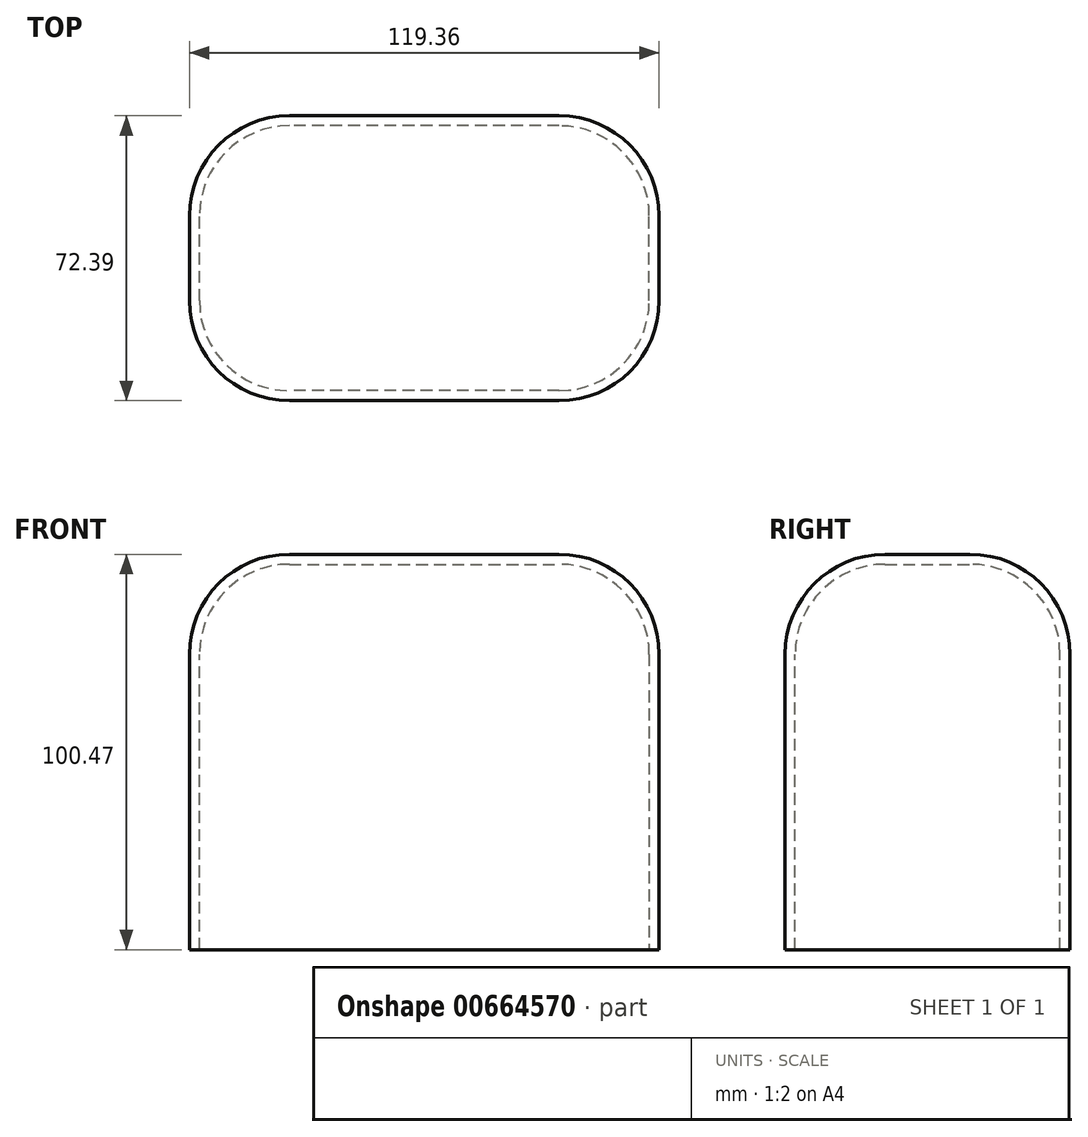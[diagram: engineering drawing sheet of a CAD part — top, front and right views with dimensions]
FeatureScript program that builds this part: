
annotation { "Feature Type Name" : "Feature", "Feature Type Description" : "" }
export const myFeature = defineFeature(function(context is Context, id is Id, definition is map)
    precondition{}
    {
        {
            var Q0;
            Q0=qCreatedBy(makeId("Front.planeOp"),FACE);
            var sketch = newSketch(context, id + "F0", { "sketchPlane" : qUnion([Q0])});
            skLineSegment(sketch, "E0", {"start": v(-68.69, 62.75) * mm, "end": v(50.67, 62.75) * mm});
            skLineSegment(sketch, "E1", {"start": v(50.67, 62.75) * mm, "end": v(50.67, -37.72) * mm});
            skLineSegment(sketch, "E2", {"start": v(50.67, -37.72) * mm, "end": v(-68.69, -37.72) * mm});
            skLineSegment(sketch, "E3", {"start": v(-68.69, -37.72) * mm, "end": v(-68.69, 62.75) * mm});
            skSolve(sketch);
        }
        {
            var Q0;
            Q0=makeQuery(id+"F0.imprint","IMPRINT",FACE,{"disambiguationData":[TD([[makeQuery(id+"F0.imprint","IMPRINT",EDGE,{"derivedFrom":sQuery(id+"F0.wireOp",EDGE,"E0")}),-1.0]])]});
            extrude(context, id + "F1", {"entities" : qUnion([Q0]), "depth" : 72.39 * mm, "offsetDistance" : 25.4 * mm});
        }
        {
            var Q0;
            Q0=makeQuery(id+"F1.opExtrude","CAP_EDGE",EDGE,{"disambiguationData":[OSD([sQuery(id+"F0.wireOp",EDGE,"E0")])],"isStart":false});
            fillet(context, id + "F2", {"entities" : qUnion([Q0]), "radius" : 25.4 * mm, "tangentPropagation" : true, "allowEdgeOverflow" : false});
        }
        {
            var Q0;
            Q0=makeQuery(id+"F1.opExtrude","CAP_EDGE",EDGE,{"disambiguationData":[OSD([sQuery(id+"F0.wireOp",EDGE,"E0")])],"isStart":true});
            fillet(context, id + "F3", {"entities" : qUnion([Q0]), "radius" : 25.4 * mm, "tangentPropagation" : true, "allowEdgeOverflow" : false});
        }
        {
            var Q0;
            Q0=makeQuery(id+"F1.opExtrude","SWEPT_EDGE",EDGE,{"disambiguationData":[OSD([sQuery(id+"F0.wireOp",EDGE,"E0"),sQuery(id+"F0.wireOp",EDGE,"E1")])]});
            fillet(context, id + "F4", {"entities" : qUnion([Q0]), "radius" : 25.4 * mm, "tangentPropagation" : true, "allowEdgeOverflow" : false});
        }
        {
            var Q0;
            Q0=makeQuery(id+"F1.opExtrude","SWEPT_EDGE",EDGE,{"disambiguationData":[OSD([sQuery(id+"F0.wireOp",EDGE,"E0"),sQuery(id+"F0.wireOp",EDGE,"E3")])]});
            fillet(context, id + "F5", {"entities" : qUnion([Q0]), "radius" : 25.4 * mm, "tangentPropagation" : true, "allowEdgeOverflow" : false});
        }
        {
            var Q0;
            Q0=makeQuery(id+"F1.opExtrude","SWEPT_FACE",FACE,{"disambiguationData":[OSD([sQuery(id+"F0.wireOp",EDGE,"E2")])]});
            shell(context, id + "F6", {"entities" : qUnion([Q0]), "thickness" : 2.54 * mm});
        }
    });
